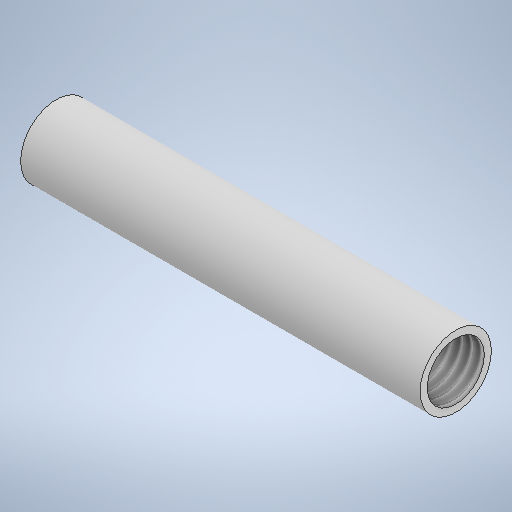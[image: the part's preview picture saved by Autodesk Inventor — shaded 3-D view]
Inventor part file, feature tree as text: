
AUTODESK INVENTOR PART (.ipt)
format: ipt  version: 2025.1 (Build 291241000, 241)  size: 242,688 bytes
history: native  units: mm
features: extrude x1, thread x1, sketch x1
ambient origin geometry x8: Origin, YZ Plane, XZ Plane, XY Plane, X Axis, Y Axis, Z Axis, Center Point
bodies: Solid1 (feature_tree)
feature tree (3):
  extrude  "Extrusion1"  Depth=28.0mm
  thread  "Thread1"  [1 undecoded]
  sketch  "Sketch1"  dims[d0=5.0mm d1=4.0mm d2=28.0mm d3=0.0mm d4=28.0mm d5=0.0mm]
note: 1 required parameter value undecoded (feature->parameter linkage not recoverable at this tier; creation-order binding heuristic only, values carry confidence <= 0.55)
